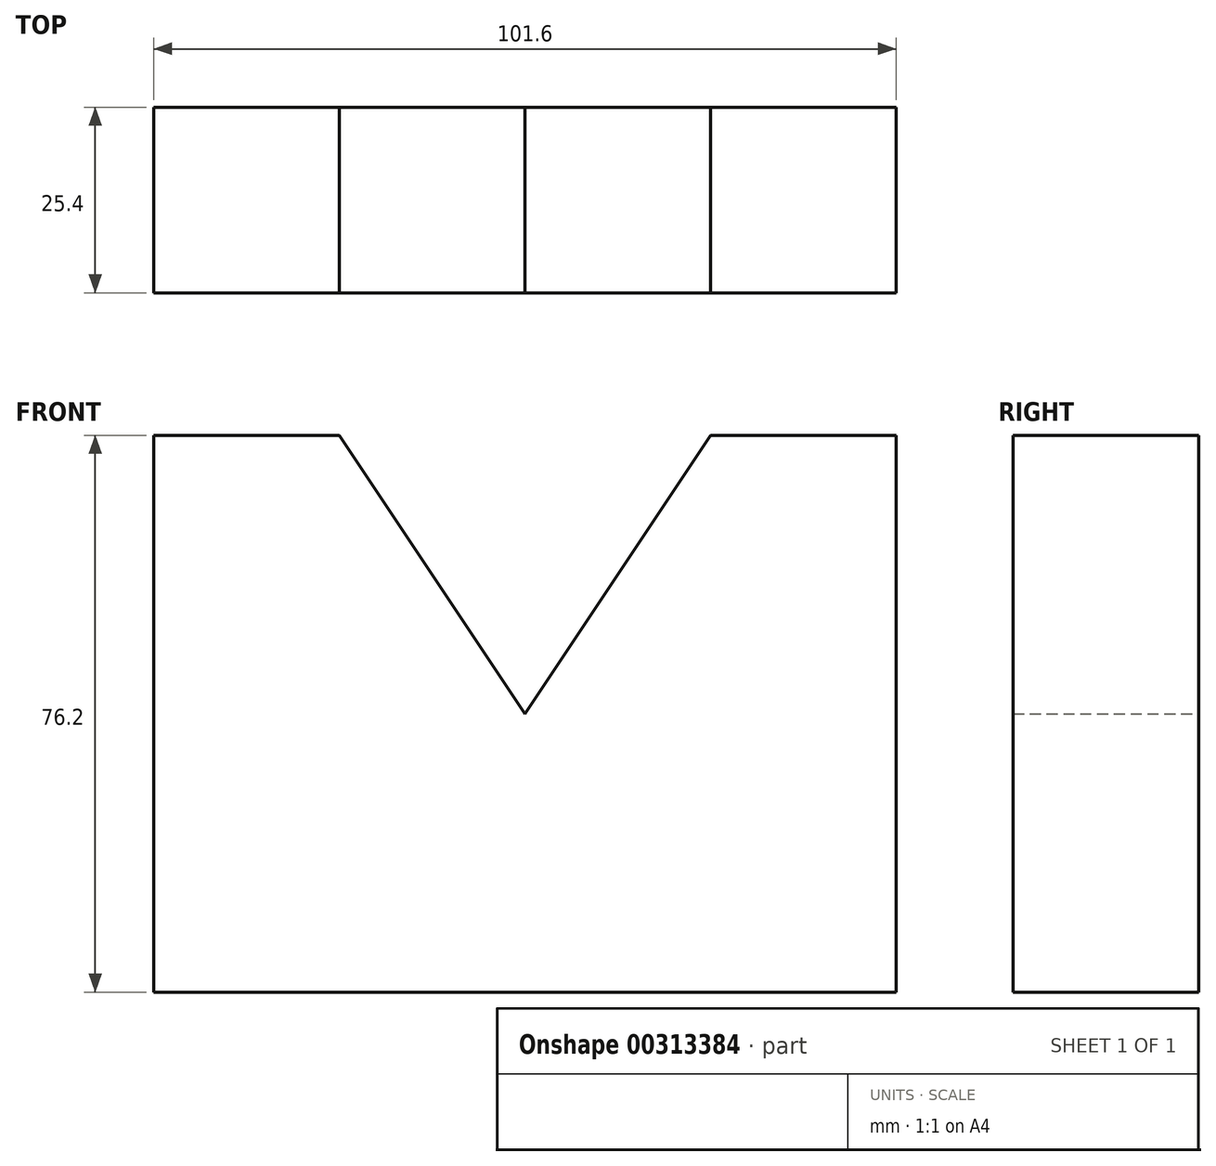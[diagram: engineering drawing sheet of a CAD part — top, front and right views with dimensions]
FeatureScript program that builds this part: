
annotation { "Feature Type Name" : "Feature", "Feature Type Description" : "" }
export const myFeature = defineFeature(function(context is Context, id is Id, definition is map)
    precondition{}
    {
        {
            var Q0;
            Q0=qCreatedBy(makeId("Front.planeOp"),FACE);
            var sketch = newSketch(context, id + "F0", { "sketchPlane" : qUnion([Q0])});
            skLineSegment(sketch, "E0", {"start": v(-50.8, -31.51) * mm, "end": v(50.8, -31.51) * mm});
            skLineSegment(sketch, "E1", {"start": v(50.8, -31.51) * mm, "end": v(50.8, 44.69) * mm});
            skLineSegment(sketch, "E2", {"start": v(50.8, 44.69) * mm, "end": v(25.4, 44.69) * mm});
            skLineSegment(sketch, "E3", {"start": v(-50.8, -31.51) * mm, "end": v(-50.8, 44.69) * mm});
            skPoint(sketch, "E3.endSnap0", {"position": v(38.1, 44.69) * mm});
            skLineSegment(sketch, "E4", {"start": v(-50.8, 44.69) * mm, "end": v(-25.4, 44.69) * mm});
            skLineSegment(sketch, "E5", {"start": v(-25.4, 44.69) * mm, "end": v(0, 6.59) * mm});
            skLineSegment(sketch, "E6", {"start": v(25.4, 44.69) * mm, "end": v(0, 6.59) * mm});
            skSolve(sketch);
        }
        {
            var Q0;
            Q0 = qSketchRegion(id + "F0", true);
            extrude(context, id + "F1", {"entities" : qUnion([Q0]), "depth" : 25.4 * mm});
        }
    });
